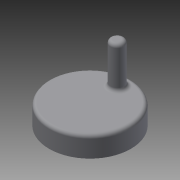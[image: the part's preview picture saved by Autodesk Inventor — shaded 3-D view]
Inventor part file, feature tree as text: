
AUTODESK INVENTOR PART (.ipt)
format: ipt  version: 2014 (Build 180170000, 170)  size: 113,152 bytes
history: native  units: in
note: dims shown in document units (in); Inventor stores cm internally (conversion verified against a paired STEP export)
features: extrude x3, sketch x3, fillet x1
ambient origin geometry x8: Origin, YZ Plane, XZ Plane, XY Plane, X Axis, Y Axis, Z Axis, Center Point
bodies: Solid1 (feature_tree)
feature tree (7):
  extrude  "Extrusion1"  Depth=0.75in TaperAngle=0.0deg
  extrude  "Extrusion2"  Depth=0.73in
  extrude  "Extrusion3"  Depth=0.125in
  fillet  "Fillet1"  Radius=0.5in
  sketch  "Sketch1"  dims[d0=3.0in d1=0.75in d2=0.0in]
  sketch  "Sketch3"  dims[d5=0.73in d6=0.73in]
  sketch  "Sketch4"  dims[d7=0.6in d8=0.0in d9=1.0in d10=0.5in d11=1.5in d12=0.0in d13=0.125in]
